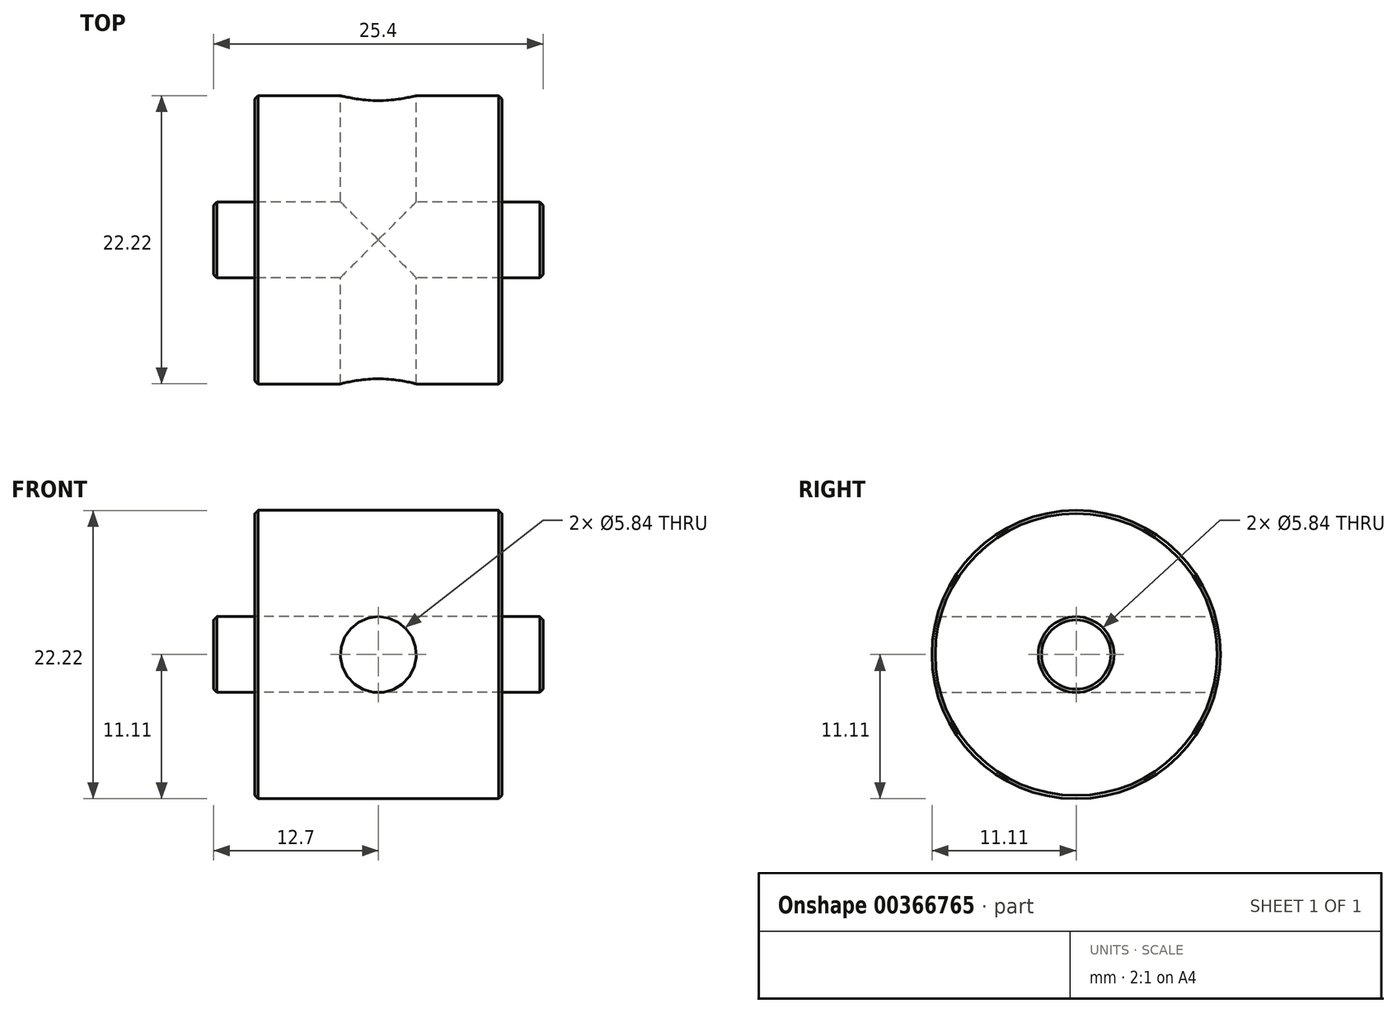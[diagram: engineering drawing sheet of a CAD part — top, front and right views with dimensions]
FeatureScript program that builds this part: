
annotation { "Feature Type Name" : "Feature", "Feature Type Description" : "" }
export const myFeature = defineFeature(function(context is Context, id is Id, definition is map)
    precondition{}
    {
        {
            var Q0;
            Q0=qCreatedBy(makeId("Front.planeOp"),FACE);
            var sketch = newSketch(context, id + "F0", { "sketchPlane" : qUnion([Q0])});
            skLineSegment(sketch, "E0.bottom", {"start": v(-12.7, 0) * mm, "end": v(12.7, 0) * mm});
            skLineSegment(sketch, "E0.top", {"start": v(-12.7, 2.92) * mm, "end": v(12.7, 2.92) * mm});
            skLineSegment(sketch, "E0.left", {"start": v(-12.7, 0) * mm, "end": v(-12.7, 2.92) * mm});
            skLineSegment(sketch, "E0.right", {"start": v(12.7, 0) * mm, "end": v(12.7, 2.92) * mm});
            skLineSegment(sketch, "E1.bottom", {"start": v(-9.52, 0) * mm, "end": v(9.53, 0) * mm});
            skLineSegment(sketch, "E1.top", {"start": v(-9.53, 11.11) * mm, "end": v(9.52, 11.11) * mm});
            skLineSegment(sketch, "E1.left", {"start": v(-9.52, 0) * mm, "end": v(-9.53, 11.11) * mm});
            skLineSegment(sketch, "E1.right", {"start": v(9.53, 0) * mm, "end": v(9.52, 11.11) * mm});
            skSolve(sketch);
        }
        {
            var Q0;
            {var subQ0=sQuery(id+"F0.wireOp",EDGE,"E0.left");Q0=makeQuery(id+"F0.imprint","IMPRINT",FACE,{"disambiguationData":[TD([[makeQuery(id+"F0.imprint","IMPRINT",EDGE,{"derivedFrom":subQ0}),-1.0]])]});}
            var Q1;
            {var subQ5=sQuery(id+"F0.wireOp",EDGE,"E1.bottom");Q1=makeQuery(id+"F0.imprint","IMPRINT",FACE,{"disambiguationData":[TD([[makeQuery(id+"F0.imprint","IMPRINT",EDGE,{"derivedFrom":subQ5}),1.0]])]});}
            var Q2;
            {var subQ0=sQuery(id+"F0.wireOp",EDGE,"E0.right");Q2=makeQuery(id+"F0.imprint","IMPRINT",FACE,{"disambiguationData":[TD([[makeQuery(id+"F0.imprint","IMPRINT",EDGE,{"derivedFrom":subQ0}),1.0]])]});}
            var Q3;
            {var subQ5=sQuery(id+"F0.wireOp",EDGE,"E1.top");Q3=makeQuery(id+"F0.imprint","IMPRINT",FACE,{"disambiguationData":[TD([[makeQuery(id+"F0.imprint","IMPRINT",EDGE,{"derivedFrom":subQ5}),-1.0]])]});}
            var Q4;
            Q4=sQuery(id+"F0.wireOp",EDGE,"E0.bottom");
            revolve(context, id + "F1", {"entities" : qUnion([Q0, Q1, Q2, Q3]), "axis" : qUnion([Q4]), "revolveType" : RevolveType.FULL});
        }
        {
            var Q0;
            Q0=qCreatedBy(makeId("Front.planeOp"),FACE);
            var sketch = newSketch(context, id + "F2", { "sketchPlane" : qUnion([Q0])});
            skCircle(sketch, "E2", {"center": v(0, 0) * mm, "radius": 2.92 * mm});
            skSolve(sketch);
        }
        {
            var Q0;
            Q0 = qSketchRegion(id + "F2", true);
            extrude(context, id + "F3", {"entities" : qUnion([Q0]), "operationType" : NewBodyOperationType.REMOVE, "endBound" : BoundingType.SYMMETRIC, "depth" : 508 * mm});
        }
        {
            var Q0;
            Q0=makeQuery(id+"F1.opRevolve","SWEPT_EDGE",EDGE,{"disambiguationData":[OSD([sQuery(id+"F0.wireOp",EDGE,"E0.top"),sQuery(id+"F0.wireOp",EDGE,"E0.left")])]});
            var Q1;
            Q1=makeQuery(id+"F1.opRevolve","SWEPT_EDGE",EDGE,{"disambiguationData":[OSD([sQuery(id+"F0.wireOp",EDGE,"E1.top"),sQuery(id+"F0.wireOp",EDGE,"E1.left")])]});
            var Q2;
            Q2=makeQuery(id+"F1.opRevolve","SWEPT_EDGE",EDGE,{"disambiguationData":[OSD([sQuery(id+"F0.wireOp",EDGE,"E1.top"),sQuery(id+"F0.wireOp",EDGE,"E1.right")])]});
            var Q3;
            Q3=makeQuery(id+"F1.opRevolve","SWEPT_EDGE",EDGE,{"disambiguationData":[OSD([sQuery(id+"F0.wireOp",EDGE,"E0.top"),sQuery(id+"F0.wireOp",EDGE,"E0.right")])]});
            chamfer(context, id + "F4", {"entities" : qUnion([Q0, Q1, Q2, Q3]), "width" : 0.25 * mm, "tangentPropagation" : true});
        }
    });
